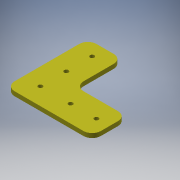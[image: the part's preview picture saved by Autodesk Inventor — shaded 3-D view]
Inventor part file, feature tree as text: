
AUTODESK INVENTOR PART (.ipt)
format: ipt  version: 2017 SP1 (Build 210196100, 196)  size: 123,904 bytes
history: native  units: in
note: dims shown in document units (in); Inventor stores cm internally (conversion verified against a paired STEP export)
features: extrude x1, fillet x1, sketch x1
ambient origin geometry x8: Origin, YZ Plane, XZ Plane, XY Plane, X Axis, Y Axis, Z Axis, Center Point
bodies: Solid1 (feature_tree)
feature tree (3):
  extrude  "Extrusion1"  Depth=0.875in
  fillet  "Fillet1"  Radius=1.0in
  sketch  "Sketch1"  dims[d0=0.125in d1=0.875in d2=1.0in d3=0.375in d4=0.75in d5=0.75in d6=0.125in d7=0.0in d8=0.25in]
